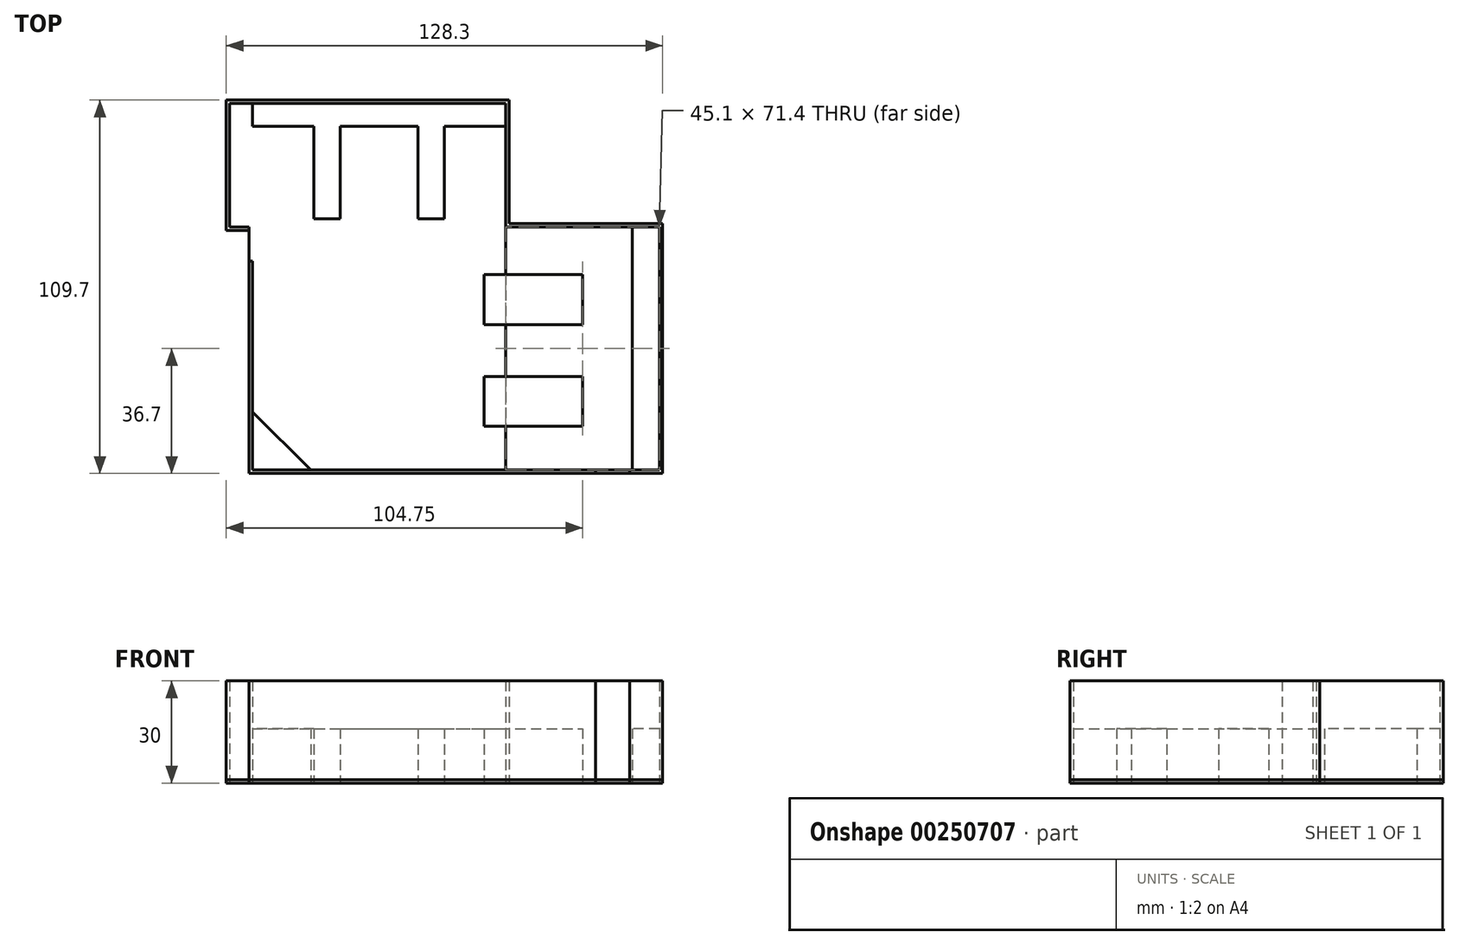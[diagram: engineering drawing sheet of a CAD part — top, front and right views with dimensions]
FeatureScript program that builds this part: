
annotation { "Feature Type Name" : "Feature", "Feature Type Description" : "" }
export const myFeature = defineFeature(function(context is Context, id is Id, definition is map)
    precondition{}
    {
        {
            var Q0;
            Q0=qCreatedBy(makeId("Top.planeOp"),FACE);
            var sketch = newSketch(context, id + "F0", { "sketchPlane" : qUnion([Q0])});
            skLineSegment(sketch, "E0.bottom", {"start": v(-74.5, 36.3) * mm, "end": v(0, 36.3) * mm});
            skLineSegment(sketch, "E0.top", {"start": v(-74.5, 0) * mm, "end": v(0, 0) * mm});
            skLineSegment(sketch, "E0.left", {"start": v(-74.5, 36.3) * mm, "end": v(-74.5, 0) * mm});
            skLineSegment(sketch, "E0.right", {"start": v(0, 36.3) * mm, "end": v(0, 0) * mm});
            skLineSegment(sketch, "E1.top", {"start": v(-74.5, -71.4) * mm, "end": v(0, -71.4) * mm});
            skLineSegment(sketch, "E1.left", {"start": v(-74.5, 0) * mm, "end": v(-74.5, -71.4) * mm});
            skLineSegment(sketch, "E1.right", {"start": v(0, 0) * mm, "end": v(0, -71.4) * mm});
            skLineSegment(sketch, "E2.bottom", {"start": v(0, -71.4) * mm, "end": v(45.1, -71.4) * mm});
            skLineSegment(sketch, "E2.top", {"start": v(0, 0) * mm, "end": v(45.1, 0) * mm});
            skLineSegment(sketch, "E2.left", {"start": v(0, -71.4) * mm, "end": v(0, 0) * mm});
            skLineSegment(sketch, "E2.right", {"start": v(45.1, -71.4) * mm, "end": v(45.1, 0) * mm});
            skLineSegment(sketch, "E3.bottom", {"start": v(-74.5, 0) * mm, "end": v(-81.2, 0) * mm});
            skLineSegment(sketch, "E3.top", {"start": v(-74.5, 36.3) * mm, "end": v(-81.2, 36.3) * mm});
            skLineSegment(sketch, "E3.left", {"start": v(-74.5, 0) * mm, "end": v(-74.5, 36.3) * mm});
            skLineSegment(sketch, "E3.right", {"start": v(-81.2, 0) * mm, "end": v(-81.2, 36.3) * mm});
            skLineSegment(sketch, "E4", {"start": v(46.1, 1) * mm, "end": v(46.1, -72.4) * mm});
            skLineSegment(sketch, "E5", {"start": v(46.1, 1) * mm, "end": v(0, 1) * mm});
            skLineSegment(sketch, "E6", {"start": v(1, 0) * mm, "end": v(1, 37.3) * mm});
            skLineSegment(sketch, "E7", {"start": v(1, 37.3) * mm, "end": v(-82.2, 37.3) * mm});
            skLineSegment(sketch, "E8", {"start": v(-82.2, 37.3) * mm, "end": v(-82.2, -1) * mm});
            skLineSegment(sketch, "E9", {"start": v(-82.2, -1) * mm, "end": v(-74.5, -1) * mm});
            skLineSegment(sketch, "E10", {"start": v(46.1, -72.4) * mm, "end": v(-75.5, -72.4) * mm});
            skLineSegment(sketch, "E11", {"start": v(-75.5, -72.4) * mm, "end": v(-75.5, 0) * mm});
            skLineSegment(sketch, "E12", {"start": v(-75.5, -10) * mm, "end": v(-74.5, -10) * mm});
            skLineSegment(sketch, "E13", {"start": v(45.1, -71.4) * mm, "end": v(45.1, -72.4) * mm});
            skLineSegment(sketch, "E14", {"start": v(36.4, -71.4) * mm, "end": v(36.4, -72.4) * mm});
            skLineSegment(sketch, "E15", {"start": v(26.4, -71.4) * mm, "end": v(26.4, -72.4) * mm});
            skSolve(sketch);
        }
        {
            var Q0;
            Q0=makeQuery(id+"F0.imprint","IMPRINT",FACE,{"disambiguationData":[TD([[makeQuery(id+"F0.imprint","IMPRINT",EDGE,{"derivedFrom":sQuery(id+"F0.wireOp",EDGE,"E3.bottom")}),-1.0]])]});
            var sketch = newSketch(context, id + "F1", { "sketchPlane" : qUnion([Q0])});
            skLineSegment(sketch, "E16", {"start": v(-56.4, 29.6) * mm, "end": v(-56.4, 2.4) * mm});
            skLineSegment(sketch, "E17", {"start": v(-56.4, 2.4) * mm, "end": v(-48.7, 2.4) * mm});
            skLineSegment(sketch, "E18", {"start": v(-48.7, 2.4) * mm, "end": v(-48.7, 29.6) * mm});
            skLineSegment(sketch, "E19", {"start": v(-25.8, 29.6) * mm, "end": v(-25.8, 2.4) * mm});
            skLineSegment(sketch, "E20", {"start": v(-25.8, 2.4) * mm, "end": v(-18.1, 2.4) * mm});
            skLineSegment(sketch, "E21", {"start": v(-18.1, 2.4) * mm, "end": v(-18.1, 29.6) * mm});
            skLineSegment(sketch, "E22", {"start": v(-56.4, 29.6) * mm, "end": v(-74.5, 29.6) * mm});
            skLineSegment(sketch, "E23", {"start": v(-48.7, 29.6) * mm, "end": v(-25.8, 29.6) * mm});
            skLineSegment(sketch, "E24", {"start": v(-18.1, 29.6) * mm, "end": v(0, 29.6) * mm});
            skLineSegment(sketch, "E25", {"start": v(-74.5, 29.6) * mm, "end": v(-74.5, 36.3) * mm});
            skLineSegment(sketch, "E26", {"start": v(-74.5, 36.3) * mm, "end": v(0, 36.3) * mm});
            skLineSegment(sketch, "E27", {"start": v(0, 36.3) * mm, "end": v(0, 29.6) * mm});
            skLineSegment(sketch, "E28", {"start": v(-74.5, -71.4) * mm, "end": v(-57.39, -71.4) * mm});
            skLineSegment(sketch, "E29", {"start": v(-74.5, -71.4) * mm, "end": v(-74.5, -54.29) * mm});
            skLineSegment(sketch, "E30", {"start": v(-74.5, -54.29) * mm, "end": v(-57.39, -71.4) * mm});
            skLineSegment(sketch, "E31.bottom", {"start": v(-6.4, -14) * mm, "end": v(22.6, -14) * mm});
            skLineSegment(sketch, "E31.top", {"start": v(-6.4, -28.7) * mm, "end": v(22.6, -28.7) * mm});
            skLineSegment(sketch, "E31.left", {"start": v(-6.4, -14) * mm, "end": v(-6.4, -28.7) * mm});
            skLineSegment(sketch, "E31.right", {"start": v(22.6, -14) * mm, "end": v(22.6, -28.7) * mm});
            skLineSegment(sketch, "E32.bottom", {"start": v(-6.4, -43.9) * mm, "end": v(22.6, -43.9) * mm});
            skLineSegment(sketch, "E32.top", {"start": v(-6.4, -58.6) * mm, "end": v(22.6, -58.6) * mm});
            skLineSegment(sketch, "E32.left", {"start": v(-6.4, -43.9) * mm, "end": v(-6.4, -58.6) * mm});
            skLineSegment(sketch, "E32.right", {"start": v(22.6, -43.9) * mm, "end": v(22.6, -58.6) * mm});
            skLineSegment(sketch, "E33.bottom", {"start": v(45.1, -71.4) * mm, "end": v(37.1, -71.4) * mm});
            skLineSegment(sketch, "E33.top", {"start": v(45.1, 0) * mm, "end": v(37.1, 0) * mm});
            skLineSegment(sketch, "E33.left", {"start": v(45.1, -71.4) * mm, "end": v(45.1, 0) * mm});
            skLineSegment(sketch, "E33.right", {"start": v(37.1, -71.4) * mm, "end": v(37.1, 0) * mm});
            skSolve(sketch);
        }
        {
            var Q0;
            Q0 = qSketchRegion(id + "F1", true);
            extrude(context, id + "F2", {"entities" : qUnion([Q0]), "depth" : 16 * mm});
        }
        {
            var Q0;
            Q0 = qSketchRegion(id + "F0", true);
            var Q1;
            {var subQ3=sQuery(id+"F0.wireOp",EDGE,"E0.top");Q1=makeQuery(id+"F0.imprint","IMPRINT",FACE,{"disambiguationData":[TD([[makeQuery(id+"F0.imprint","IMPRINT",EDGE,{"derivedFrom":subQ3}),-1.0]])]});}
            var Q2;
            {var subQ3=sQuery(id+"F0.wireOp",EDGE,"E0.bottom");Q2=makeQuery(id+"F0.imprint","IMPRINT",FACE,{"disambiguationData":[TD([[makeQuery(id+"F0.imprint","IMPRINT",EDGE,{"derivedFrom":subQ3}),-1.0]])]});}
            var Q3;
            Q3=makeQuery(id+"F0.imprint","IMPRINT",FACE,{"disambiguationData":[TD([[makeQuery(id+"F0.imprint","IMPRINT",EDGE,{"derivedFrom":sQuery(id+"F0.wireOp",EDGE,"E3.top")}),1.0]])]});
            var Q4;
            {var subQ0=sQuery(id+"F0.wireOp",EDGE,"E2.left");Q4=makeQuery(id+"F0.imprint","IMPRINT",FACE,{"disambiguationData":[TD([[makeQuery(id+"F0.imprint","IMPRINT",EDGE,{"derivedFrom":subQ0}),-1.0]])]});}
            extrude(context, id + "F3", {"entities" : qUnion([Q0, Q1, Q2, Q3, Q4]), "depth" : 1 * mm});
        }
        {
            var Q0;
            {var subQ5=sQuery(id+"F0.wireOp",EDGE,"E1.top");Q0=makeQuery(id+"F0.imprint","IMPRINT",FACE,{"disambiguationData":[TD([[makeQuery(id+"F0.imprint","IMPRINT",EDGE,{"derivedFrom":subQ5}),-1.0]])]});}
            var Q1;
            {var subQ0=sQuery(id+"F0.wireOp",EDGE,"E13");Q1=makeQuery(id+"F0.imprint","IMPRINT",FACE,{"disambiguationData":[TD([[makeQuery(id+"F0.imprint","IMPRINT",EDGE,{"derivedFrom":subQ0}),-1.0]])]});}
            var Q2;
            {var subQ4=sQuery(id+"F0.wireOp",EDGE,"E2.right");Q2=makeQuery(id+"F0.imprint","IMPRINT",FACE,{"disambiguationData":[TD([[makeQuery(id+"F0.imprint","IMPRINT",EDGE,{"derivedFrom":subQ4}),-1.0]])]});}
            var Q3;
            {var subQ1=sQuery(id+"F0.wireOp",EDGE,"E0.right");var subQ3=sQuery(id+"F0.wireOp",EDGE,"E5");var subQ4=makeQuery(id+"F0.imprint","INTERSECT",VERTEX,{"derivedFrom":[subQ1,subQ3]});Q3=makeQuery(id+"F0.imprint","IMPRINT",FACE,{"disambiguationData":[TD([[makeQuery(id+"F0.imprint","IMPRINT",EDGE,{"disambiguationData":[TD([[subQ4,1.0]])],"derivedFrom":subQ3}),1.0]])]});}
            var Q4;
            {var subQ11=sQuery(id+"F0.wireOp",EDGE,"E0.bottom");Q4=makeQuery(id+"F0.imprint","IMPRINT",FACE,{"disambiguationData":[TD([[makeQuery(id+"F0.imprint","IMPRINT",EDGE,{"derivedFrom":subQ11}),1.0]])]});}
            extrude(context, id + "F4", {"entities" : qUnion([Q0, Q1, Q2, Q3, Q4]), "depth" : 30 * mm});
        }
    });
